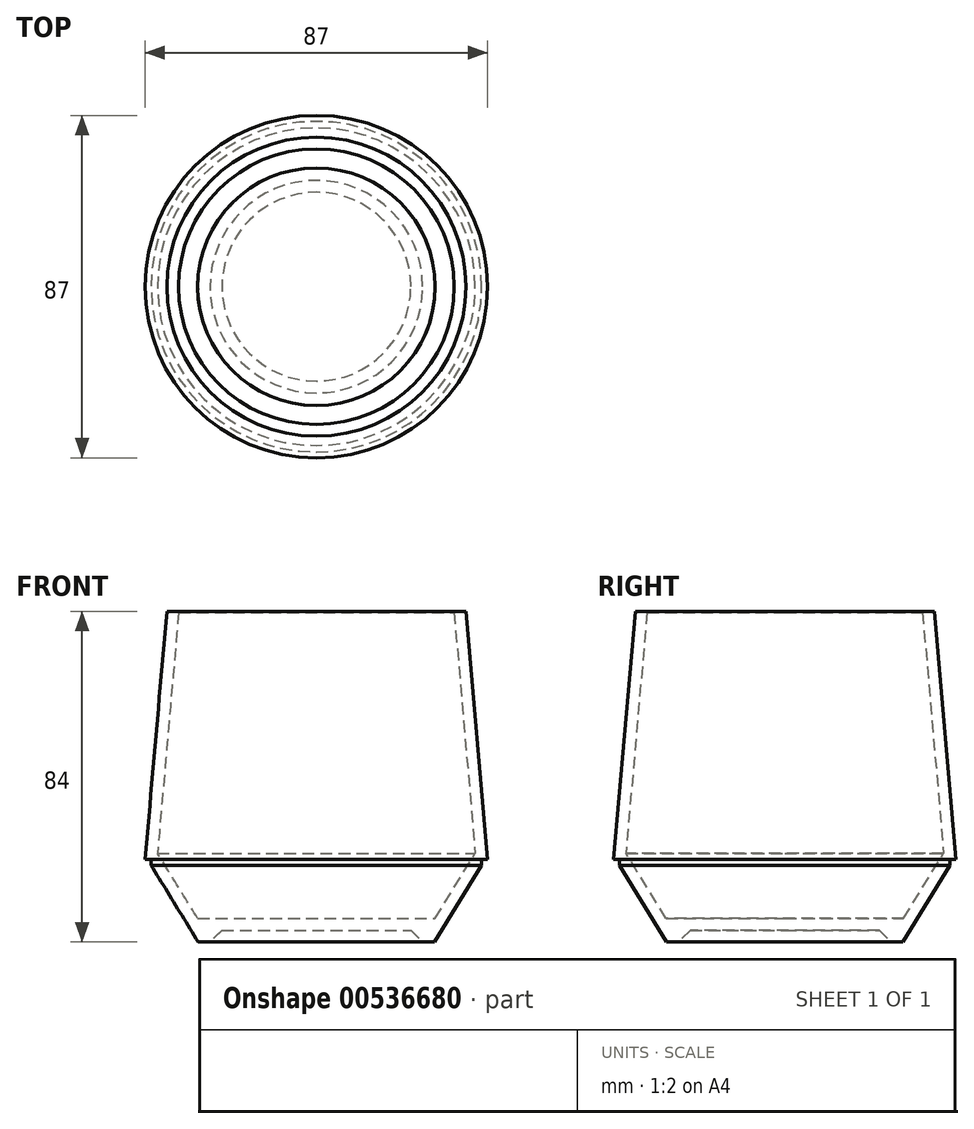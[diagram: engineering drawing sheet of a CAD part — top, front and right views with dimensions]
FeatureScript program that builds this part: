
annotation { "Feature Type Name" : "Feature", "Feature Type Description" : "" }
export const myFeature = defineFeature(function(context is Context, id is Id, definition is map)
    precondition{}
    {
        {
            var Q0;
            Q0=qCreatedBy(makeId("Front.planeOp"),FACE);
            var sketch = newSketch(context, id + "F0", { "sketchPlane" : qUnion([Q0])});
            skLineSegment(sketch, "E0", {"start": v(0, 3) * mm, "end": v(24, 3) * mm});
            skLineSegment(sketch, "E1", {"start": v(24, 3) * mm, "end": v(27, 0) * mm});
            skLineSegment(sketch, "E2", {"start": v(27, 0) * mm, "end": v(30, 0) * mm});
            skLineSegment(sketch, "E3", {"start": v(30, 0) * mm, "end": v(42, 19.5) * mm});
            skLineSegment(sketch, "E4", {"start": v(43.5, 21) * mm, "end": v(37.99, 84) * mm});
            skLineSegment(sketch, "E5", {"start": v(35, 83.74) * mm, "end": v(40.35, 22.55) * mm});
            skLineSegment(sketch, "E6", {"start": v(40.35, 22.55) * mm, "end": v(30.17, 6) * mm});
            skLineSegment(sketch, "E7", {"start": v(30.17, 6) * mm, "end": v(0, 6) * mm});
            skLineSegment(sketch, "E8", {"start": v(0, 6) * mm, "end": v(0, 3) * mm});
            skPoint(sketch, "E9.visualSharp", {"position": v(24, 3) * mm});
            skPoint(sketch, "E10.visualSharp", {"position": v(40.35, 22.55) * mm});
            skLineSegment(sketch, "E11", {"start": v(0, 0) * mm, "end": v(0, 84) * mm, "construction": true});
            skLineSegment(sketch, "E12", {"start": v(42, 19.5) * mm, "end": v(42, 21) * mm});
            skLineSegment(sketch, "E13", {"start": v(43.5, 0) * mm, "end": v(43.5, 84) * mm, "construction": true});
            skLineSegment(sketch, "E14", {"start": v(35, 83.74) * mm, "end": v(37.99, 84) * mm});
            skLineSegment(sketch, "E15", {"start": v(42, 21) * mm, "end": v(43.5, 21) * mm});
            skSolve(sketch);
        }
        {
            var Q0;
            Q0=qSketchRegion(id+"F0",true);
            var Q1;
            Q1=sQuery(id+"F0.wireOp",EDGE,"E11");
            revolve(context, id + "F1", {"entities" : qUnion([Q0]), "axis" : qUnion([Q1]), "revolveType" : RevolveType.FULL});
        }
    });
